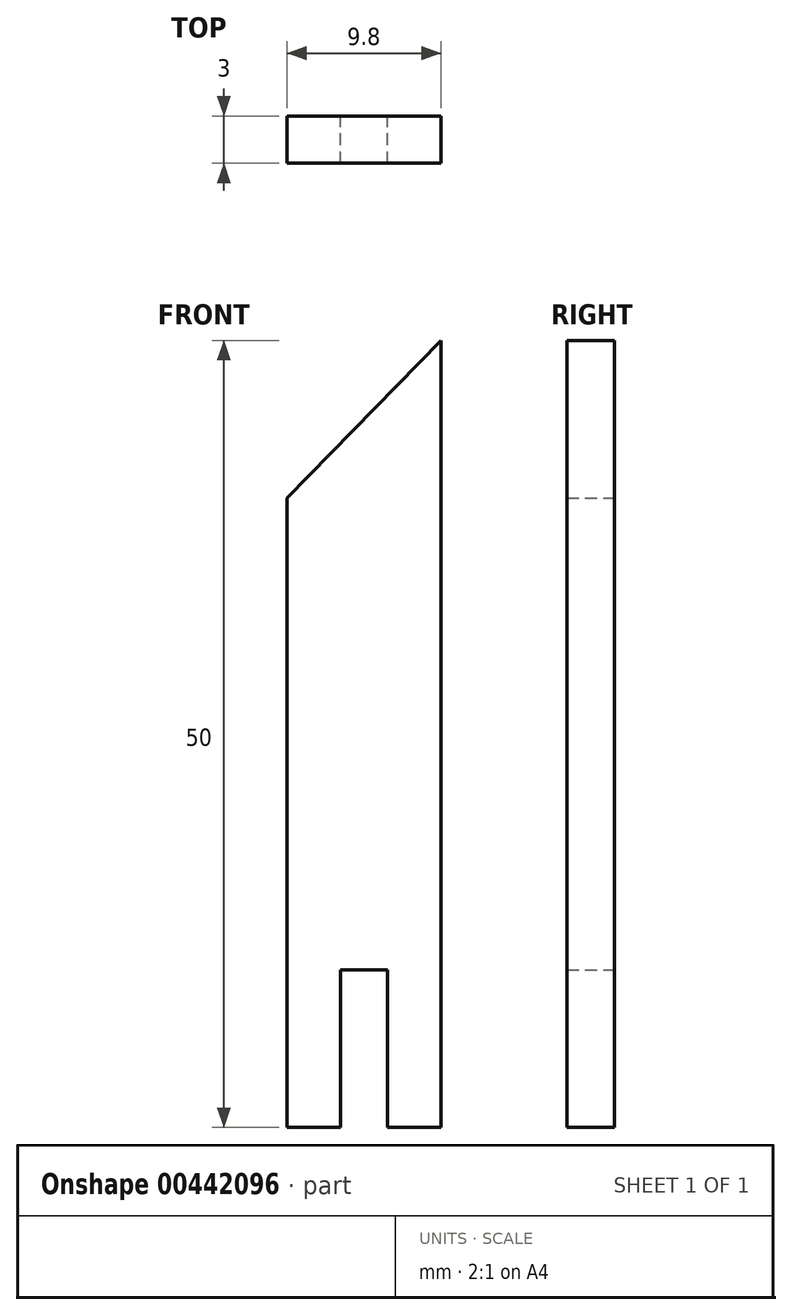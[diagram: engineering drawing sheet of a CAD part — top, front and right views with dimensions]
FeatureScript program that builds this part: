
annotation { "Feature Type Name" : "Feature", "Feature Type Description" : "" }
export const myFeature = defineFeature(function(context is Context, id is Id, definition is map)
    precondition{}
    {
        {
            var Q0;
            Q0=qCreatedBy(makeId("Front.planeOp"),FACE);
            var sketch = newSketch(context, id + "F0", { "sketchPlane" : qUnion([Q0])});
            skLineSegment(sketch, "E0", {"start": v(-9.8, 0) * mm, "end": v(-9.8, 40) * mm});
            skLineSegment(sketch, "E1", {"start": v(-9.8, 40) * mm, "end": v(0, 50) * mm});
            skLineSegment(sketch, "E2", {"start": v(0, 50) * mm, "end": v(0, 0) * mm});
            skLineSegment(sketch, "E3", {"start": v(0, 0) * mm, "end": v(-3.4, 0) * mm});
            skLineSegment(sketch, "E4.bottom", {"start": v(-3.4, 10) * mm, "end": v(-6.4, 10) * mm});
            skLineSegment(sketch, "E4.left", {"start": v(-3.4, 10) * mm, "end": v(-3.4, 0) * mm});
            skLineSegment(sketch, "E4.right", {"start": v(-6.4, 10) * mm, "end": v(-6.4, 0) * mm});
            skPoint(sketch, "E4.middle", {"position": v(-4.9, 0) * mm});
            skPoint(sketch, "E4.top.end.orphan", {"position": v(-6.4, -10) * mm});
            skPoint(sketch, "E4.top.start.orphan", {"position": v(-3.4, -10) * mm});
            skLineSegment(sketch, "E5.trimOffspring", {"start": v(-6.4, 0) * mm, "end": v(-9.8, 0) * mm});
            skSolve(sketch);
        }
        {
            var Q0;
            Q0 = qSketchRegion(id + "F0", true);
            extrude(context, id + "F1", {"entities" : qUnion([Q0]), "depth" : 3 * mm});
        }
    });
